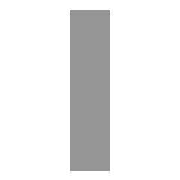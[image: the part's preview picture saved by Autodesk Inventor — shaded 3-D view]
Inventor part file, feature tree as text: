
AUTODESK INVENTOR PART (.ipt)
format: ipt  version: 2024 (Build 280153000, 153)  size: 117,760 bytes
history: native  units: mm (DEFAULTED — no unit token found)
features: other x4, sketch x3, hole x2, plane x1
ambient origin geometry x8: Origin, YZ Plane, XZ Plane, XY Plane, X Axis, Y Axis, Z Axis, Center Point
bodies: Solid1 (feature_tree), Body (feature_tree)
feature tree (10):
  parser-record x1  (decoder bookkeeping rows leaked as tree rows — omitted from the tree; the rows remain in map.json)
  other  "Driven Length"
  other  "Start Plane"
  other  "End Plane"
  hole  "Hole1"  [1 undecoded]
  hole  "Hole2"  [1 undecoded]
  sketch  "Sketch3"  dims[d0=200.0mm d1=15.0mm]
  plane  "Work Plane3"
  sketch  "Sketch5"  dims[d2=125.0mm d3=0.0mm]
  sketch  "Sketch6"  dims[d4=7.5mm d5=100.0mm d6=-0.0mm d7=125.0mm d8=90.0deg d9=125.0mm d10=17.5mm d11=6.0mm d12=4.0mm d13=2.0mm d14=90.0deg d15=8.0mm d16=0.0mm d17=17.5mm d18=6.0mm d19=4.0mm d20=2.0mm d21=90.0deg d22=8.0mm d23=0.0mm]
note: 2 required parameter values undecoded (feature->parameter linkage not recoverable at this tier; creation-order binding heuristic only, values carry confidence <= 0.55)
